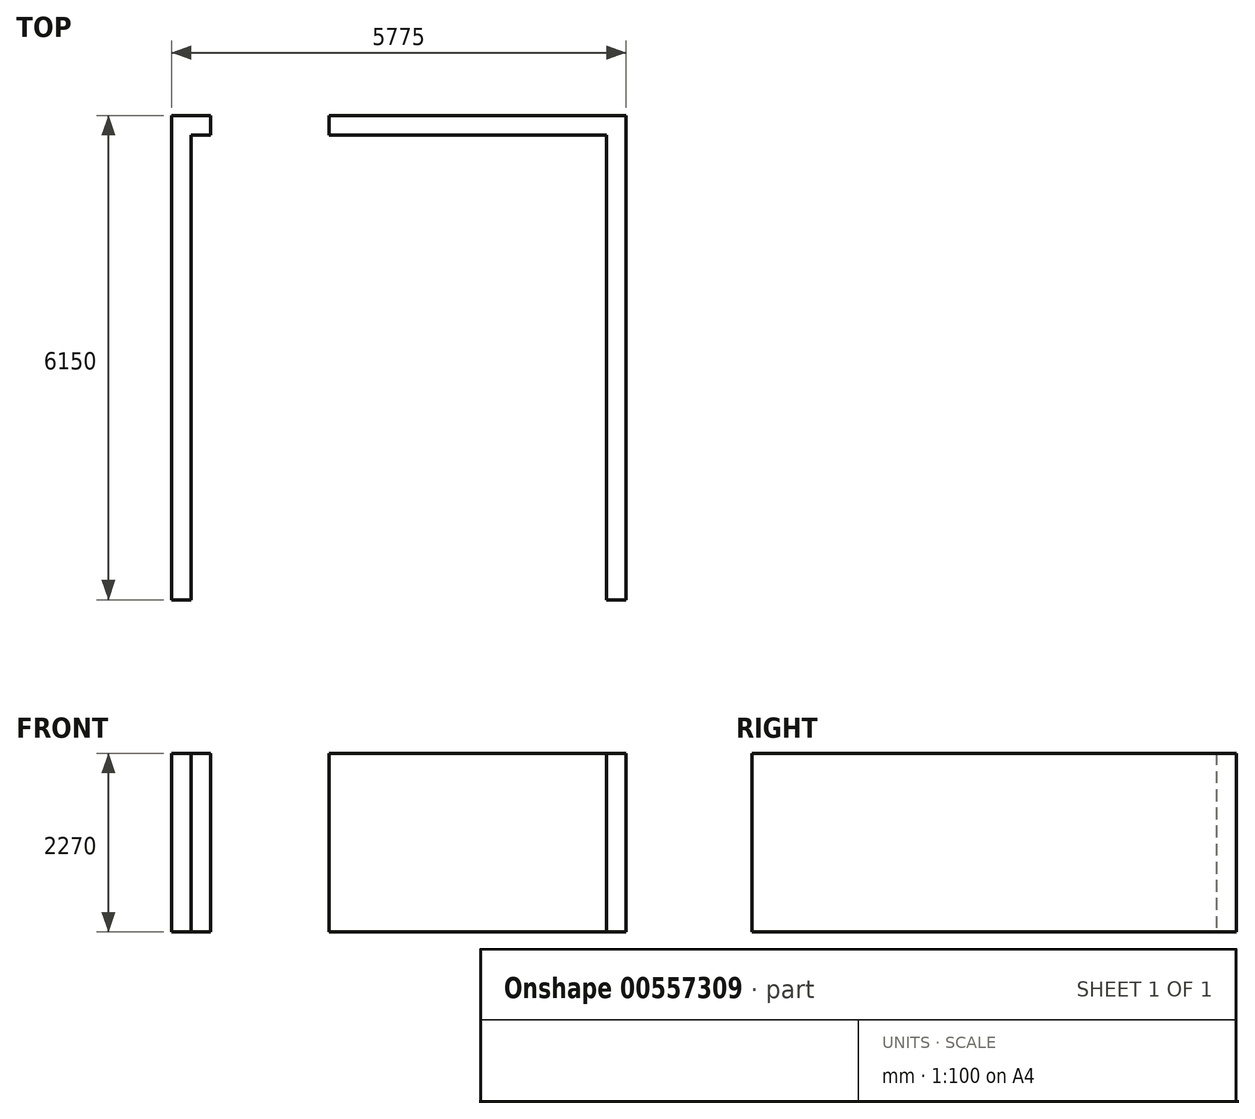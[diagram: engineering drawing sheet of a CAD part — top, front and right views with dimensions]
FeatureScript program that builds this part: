
annotation { "Feature Type Name" : "Feature", "Feature Type Description" : "" }
export const myFeature = defineFeature(function(context is Context, id is Id, definition is map)
    precondition{}
    {
        {
            var Q0;
            Q0=qCreatedBy(makeId("Top.planeOp"),FACE);
            var sketch = newSketch(context, id + "F0", { "sketchPlane" : qUnion([Q0])});
            skLineSegment(sketch, "E0.bottom", {"start": v(-2637.5, 2950) * mm, "end": v(-2387.5, 2950) * mm});
            skLineSegment(sketch, "E0.left", {"start": v(-2637.5, 2950) * mm, "end": v(-2637.5, -2950) * mm});
            skLineSegment(sketch, "E0.right", {"start": v(2637.5, 2950) * mm, "end": v(2637.5, -2950) * mm});
            skPoint(sketch, "E0.middle", {"position": v(0, 0) * mm});
            skLineSegment(sketch, "E1.bottom", {"start": v(-2887.5, -2950) * mm, "end": v(-2637.5, -2950) * mm});
            skLineSegment(sketch, "E1.top", {"start": v(-2887.5, 3200) * mm, "end": v(-2387.5, 3200) * mm});
            skLineSegment(sketch, "E1.left", {"start": v(-2887.5, -2950) * mm, "end": v(-2887.5, 3200) * mm});
            skLineSegment(sketch, "E1.right", {"start": v(2887.5, -2950) * mm, "end": v(2887.5, 3200) * mm});
            skLineSegment(sketch, "E2", {"start": v(-2387.5, 2950) * mm, "end": v(-2387.5, 3200) * mm});
            skLineSegment(sketch, "E3", {"start": v(-887.5, 2950) * mm, "end": v(-887.5, 3200) * mm});
            skLineSegment(sketch, "E4.trimOffspring", {"start": v(-887.5, 3200) * mm, "end": v(2887.5, 3200) * mm});
            skLineSegment(sketch, "E5.trimOffspring", {"start": v(-887.5, 2950) * mm, "end": v(2637.5, 2950) * mm});
            skLineSegment(sketch, "E6.trimOffspring", {"start": v(2637.5, -2950) * mm, "end": v(2887.5, -2950) * mm});
            skSolve(sketch);
        }
        {
            var Q0;
            Q0=makeQuery(id+"F0.imprint","IMPRINT",FACE,{"disambiguationData":[TD([[makeQuery(id+"F0.imprint","IMPRINT",EDGE,{"derivedFrom":sQuery(id+"F0.wireOp",EDGE,"E0.bottom")}),1.0]])]});
            var Q1;
            Q1=makeQuery(id+"F0.imprint","IMPRINT",FACE,{"disambiguationData":[TD([[makeQuery(id+"F0.imprint","IMPRINT",EDGE,{"derivedFrom":sQuery(id+"F0.wireOp",EDGE,"E0.right")}),1.0]])]});
            extrude(context, id + "F1", {"entities" : qUnion([Q0, Q1]), "depth" : 2270 * mm, "offsetDistance" : 25 * mm});
        }
    });
